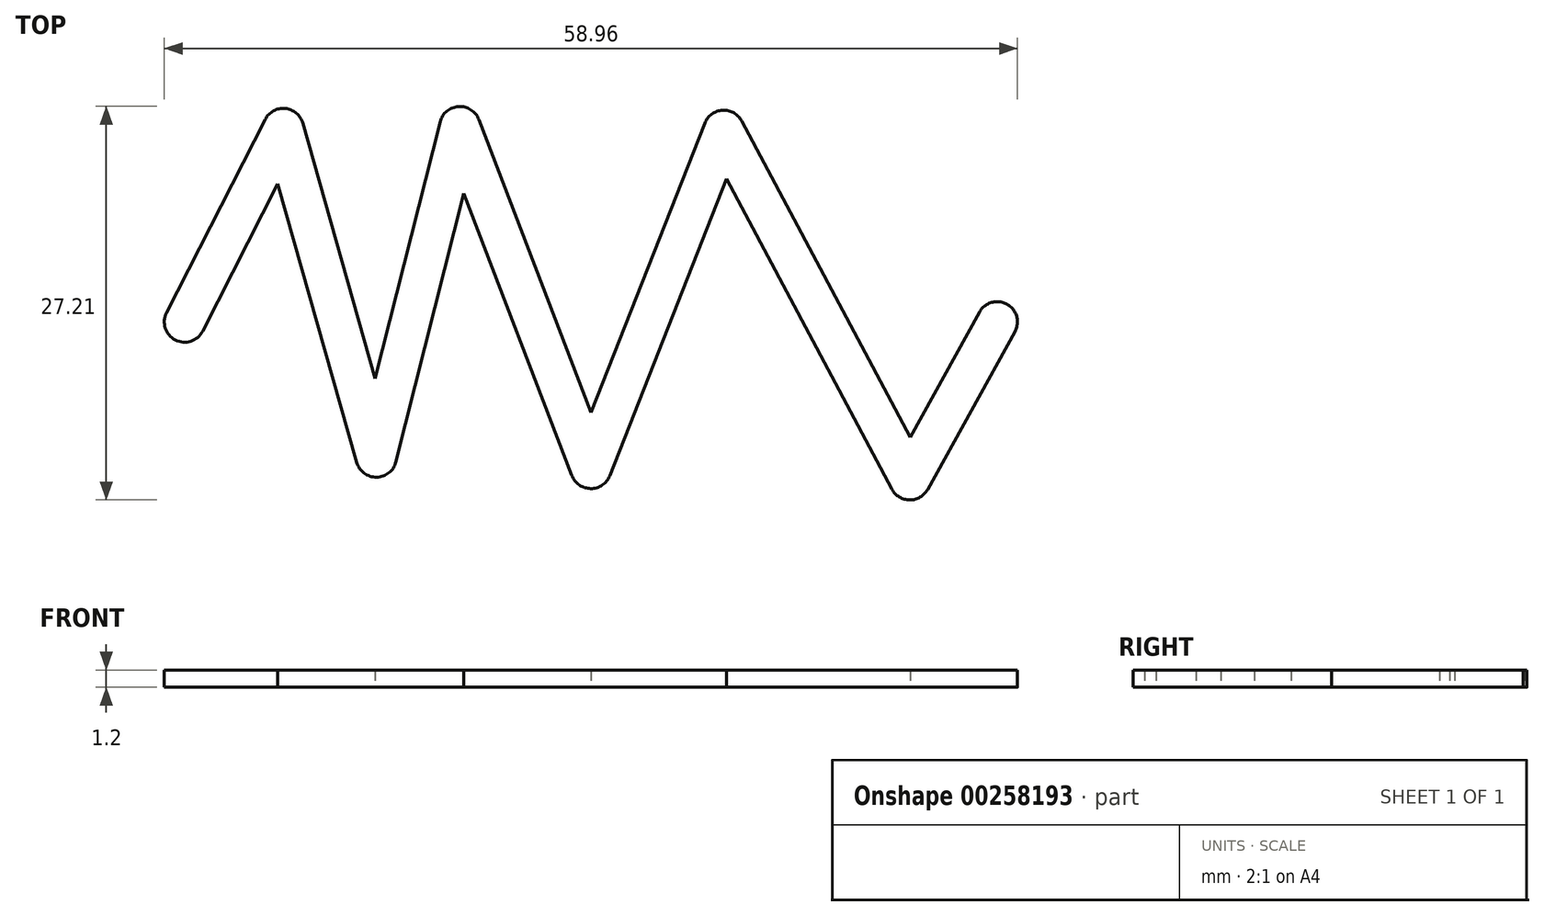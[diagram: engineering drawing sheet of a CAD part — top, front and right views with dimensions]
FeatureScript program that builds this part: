
annotation { "Feature Type Name" : "Feature", "Feature Type Description" : "" }
export const myFeature = defineFeature(function(context is Context, id is Id, definition is map)
    precondition{}
    {
        {
            var Q0;
            Q0=qCreatedBy(makeId("Top.planeOp"),FACE);
            var sketch = newSketch(context, id + "F0", { "sketchPlane" : qUnion([Q0])});
            skLineSegment(sketch, "E0", {"start": v(-42.58, 0) * mm, "end": v(-29.6, 0) * mm});
            skLineSegment(sketch, "E1", {"start": v(-29.6, 0) * mm, "end": v(-22.77, 13.37) * mm});
            skLineSegment(sketch, "E2", {"start": v(-22.77, 13.37) * mm, "end": v(-16.34, -9.33) * mm});
            skLineSegment(sketch, "E3", {"start": v(-16.34, -9.33) * mm, "end": v(-10.57, 13.5) * mm});
            skLineSegment(sketch, "E4", {"start": v(-10.57, 13.5) * mm, "end": v(-1.51, -10.12) * mm});
            skLineSegment(sketch, "E5", {"start": v(-1.51, -10.12) * mm, "end": v(7.67, 13.23) * mm});
            skLineSegment(sketch, "E6", {"start": v(7.67, 13.23) * mm, "end": v(20.53, -10.9) * mm});
            skLineSegment(sketch, "E7", {"start": v(20.53, -10.9) * mm, "end": v(26.57, 0) * mm});
            skLineSegment(sketch, "E8", {"start": v(26.57, 0) * mm, "end": v(42.18, 0) * mm});
            skArc(sketch, "E9.0.startCap", {"start": v(-24.12, 12.98) * mm, "mid": v(-23.15, 14.71) * mm, "end": v(-21.42, 13.75) * mm});
            skArc(sketch, "E9.0.endCap", {"start": v(-15, -8.95) * mm, "mid": v(-15.96, -10.68) * mm, "end": v(-17.69, -9.72) * mm});
            skLineSegment(sketch, "E9.0.left", {"start": v(-21.42, 13.75) * mm, "end": v(-15, -8.95) * mm});
            skLineSegment(sketch, "E9.0.right", {"start": v(-24.12, 12.98) * mm, "end": v(-17.69, -9.72) * mm});
            skArc(sketch, "E9.1.startCap", {"start": v(21.76, -11.59) * mm, "mid": v(19.85, -12.13) * mm, "end": v(19.3, -10.23) * mm});
            skArc(sketch, "E9.1.endCap", {"start": v(25.34, 0.68) * mm, "mid": v(27.25, 1.22) * mm, "end": v(27.8, -0.68) * mm});
            skLineSegment(sketch, "E9.1.left", {"start": v(19.3, -10.23) * mm, "end": v(25.34, 0.68) * mm});
            skLineSegment(sketch, "E9.1.right", {"start": v(21.76, -11.59) * mm, "end": v(27.8, -0.68) * mm});
            skArc(sketch, "E9.2.startCap", {"start": v(6.44, 12.58) * mm, "mid": v(7.02, 14.47) * mm, "end": v(8.9, 13.9) * mm});
            skArc(sketch, "E9.2.endCap", {"start": v(21.77, -10.25) * mm, "mid": v(21.2, -12.14) * mm, "end": v(19.3, -11.57) * mm});
            skLineSegment(sketch, "E9.2.left", {"start": v(8.9, 13.9) * mm, "end": v(21.77, -10.25) * mm});
            skLineSegment(sketch, "E9.2.right", {"start": v(6.44, 12.58) * mm, "end": v(19.3, -11.57) * mm});
            skArc(sketch, "E9.3.startCap", {"start": v(-14.98, -9.68) * mm, "mid": v(-16.68, -10.7) * mm, "end": v(-17.7, -9) * mm});
            skArc(sketch, "E9.3.endCap", {"start": v(-11.92, 13.84) * mm, "mid": v(-10.22, 14.85) * mm, "end": v(-9.2, 13.15) * mm});
            skLineSegment(sketch, "E9.3.left", {"start": v(-17.7, -9) * mm, "end": v(-11.92, 13.84) * mm});
            skLineSegment(sketch, "E9.3.right", {"start": v(-14.98, -9.68) * mm, "end": v(-9.2, 13.15) * mm});
            skArc(sketch, "E9.4.startCap", {"start": v(-0.2, -10.63) * mm, "mid": v(-2.02, -11.42) * mm, "end": v(-2.81, -9.6) * mm});
            skArc(sketch, "E9.4.endCap", {"start": v(6.37, 13.75) * mm, "mid": v(8.19, 14.54) * mm, "end": v(8.98, 12.72) * mm});
            skLineSegment(sketch, "E9.4.left", {"start": v(-2.81, -9.6) * mm, "end": v(6.37, 13.75) * mm});
            skLineSegment(sketch, "E9.4.right", {"start": v(-0.2, -10.63) * mm, "end": v(8.98, 12.72) * mm});
            skArc(sketch, "E9.5.startCap", {"start": v(26.57, -1.4) * mm, "mid": v(25.17, 0) * mm, "end": v(26.57, 1.4) * mm});
            skArc(sketch, "E9.5.endCap", {"start": v(42.18, 1.4) * mm, "mid": v(43.58, 0) * mm, "end": v(42.18, -1.4) * mm});
            skLineSegment(sketch, "E9.5.left", {"start": v(26.57, 1.4) * mm, "end": v(42.18, 1.4) * mm});
            skLineSegment(sketch, "E9.5.right", {"start": v(26.57, -1.4) * mm, "end": v(42.18, -1.4) * mm});
            skArc(sketch, "E9.6.startCap", {"start": v(-11.87, 13) * mm, "mid": v(-11.07, 14.8) * mm, "end": v(-9.26, 14) * mm});
            skArc(sketch, "E9.6.endCap", {"start": v(-0.2, -9.62) * mm, "mid": v(-1.01, -11.43) * mm, "end": v(-2.82, -10.62) * mm});
            skLineSegment(sketch, "E9.6.left", {"start": v(-9.26, 14) * mm, "end": v(-0.2, -9.62) * mm});
            skLineSegment(sketch, "E9.6.right", {"start": v(-11.87, 13) * mm, "end": v(-2.82, -10.62) * mm});
            skArc(sketch, "E9.7.startCap", {"start": v(-28.34, -0.64) * mm, "mid": v(-30.23, -1.25) * mm, "end": v(-30.84, 0.64) * mm});
            skArc(sketch, "E9.7.endCap", {"start": v(-24.02, 14) * mm, "mid": v(-22.13, 14.61) * mm, "end": v(-21.52, 12.73) * mm});
            skLineSegment(sketch, "E9.7.left", {"start": v(-30.84, 0.64) * mm, "end": v(-24.02, 14) * mm});
            skLineSegment(sketch, "E9.7.right", {"start": v(-28.34, -0.64) * mm, "end": v(-21.52, 12.73) * mm});
            skArc(sketch, "E9.8.startCap", {"start": v(-42.58, -1.4) * mm, "mid": v(-43.98, 0) * mm, "end": v(-42.58, 1.4) * mm});
            skArc(sketch, "E9.8.endCap", {"start": v(-29.6, 1.4) * mm, "mid": v(-28.2, 0) * mm, "end": v(-29.6, -1.4) * mm});
            skLineSegment(sketch, "E9.8.left", {"start": v(-42.58, 1.4) * mm, "end": v(-29.6, 1.4) * mm});
            skLineSegment(sketch, "E9.8.right", {"start": v(-42.58, -1.4) * mm, "end": v(-29.6, -1.4) * mm});
            skSolve(sketch);
        }
        {
            var Q0;
            {var subQ1=sQuery(id+"F0.wireOp",EDGE,"E9.2.startCap");Q0=makeQuery(id+"F0.imprint","IMPRINT",FACE,{"disambiguationData":[TD([[makeQuery(id+"F0.imprint","IMPRINT",EDGE,{"derivedFrom":subQ1}),1.0]])]});}
            var Q1;
            {var subQ0=sQuery(id+"F0.wireOp",EDGE,"E9.2.left");var subQ3=sQuery(id+"F0.wireOp",EDGE,"E7");var subQ4=makeQuery(id+"F0.imprint","INTERSECT",VERTEX,{"derivedFrom":[subQ3,subQ0]});Q1=makeQuery(id+"F0.imprint","IMPRINT",FACE,{"disambiguationData":[TD([[makeQuery(id+"F0.imprint","IMPRINT",EDGE,{"disambiguationData":[TD([[subQ4,-1.0]])],"derivedFrom":subQ3}),-1.0]])]});}
            var Q2;
            {var subQ0=sQuery(id+"F0.wireOp",EDGE,"E9.1.startCap");Q2=makeQuery(id+"F0.imprint","IMPRINT",FACE,{"disambiguationData":[TD([[makeQuery(id+"F0.imprint","IMPRINT",EDGE,{"derivedFrom":subQ0}),-1.0]])]});}
            var Q3;
            {var subQ0=sQuery(id+"F0.wireOp",EDGE,"E5");var subQ1=sQuery(id+"F0.wireOp",EDGE,"E4");var subQ2=makeQuery(id+"F0.imprint","INTERSECT",VERTEX,{"derivedFrom":[subQ1,subQ0]});Q3=makeQuery(id+"F0.imprint","IMPRINT",FACE,{"disambiguationData":[TD([[makeQuery(id+"F0.imprint","IMPRINT",EDGE,{"disambiguationData":[TD([[subQ2,1.0]])],"derivedFrom":subQ1}),1.0]])]});}
            var Q4;
            {var subQ0=sQuery(id+"F0.wireOp",EDGE,"E7");var subQ1=sQuery(id+"F0.wireOp",EDGE,"E6");var subQ2=makeQuery(id+"F0.imprint","INTERSECT",VERTEX,{"derivedFrom":[subQ1,subQ0]});Q4=makeQuery(id+"F0.imprint","IMPRINT",FACE,{"disambiguationData":[TD([[makeQuery(id+"F0.imprint","IMPRINT",EDGE,{"disambiguationData":[TD([[subQ2,1.0]])],"derivedFrom":subQ1}),1.0]])]});}
            var Q5;
            {var subQ3=sQuery(id+"F0.wireOp",EDGE,"E9.6.left");var subQ7=sQuery(id+"F0.wireOp",EDGE,"E5");var subQ9=makeQuery(id+"F0.imprint","INTERSECT",VERTEX,{"derivedFrom":[subQ7,subQ3]});Q5=makeQuery(id+"F0.imprint","IMPRINT",FACE,{"disambiguationData":[TD([[makeQuery(id+"F0.imprint","IMPRINT",EDGE,{"disambiguationData":[TD([[subQ9,-1.0]])],"derivedFrom":subQ7}),-1.0]])]});}
            var Q6;
            {var subQ2=sQuery(id+"F0.wireOp",EDGE,"E7");var subQ6=sQuery(id+"F0.wireOp",EDGE,"E8");var subQ8=makeQuery(id+"F0.imprint","INTERSECT",VERTEX,{"derivedFrom":[subQ2,subQ6]});Q6=makeQuery(id+"F0.imprint","IMPRINT",FACE,{"disambiguationData":[TD([[makeQuery(id+"F0.imprint","IMPRINT",EDGE,{"disambiguationData":[TD([[subQ8,1.0]])],"derivedFrom":subQ2}),1.0]])]});}
            var Q7;
            {var subQ0=sQuery(id+"F0.wireOp",EDGE,"E9.2.left");var subQ1=sQuery(id+"F0.wireOp",EDGE,"E7");var subQ2=makeQuery(id+"F0.imprint","INTERSECT",VERTEX,{"derivedFrom":[subQ1,subQ0]});Q7=makeQuery(id+"F0.imprint","IMPRINT",FACE,{"disambiguationData":[TD([[makeQuery(id+"F0.imprint","IMPRINT",EDGE,{"disambiguationData":[TD([[subQ2,-1.0]])],"derivedFrom":subQ1}),1.0]])]});}
            var Q8;
            {var subQ0=sQuery(id+"F0.wireOp",EDGE,"E9.2.startCap");Q8=makeQuery(id+"F0.imprint","IMPRINT",FACE,{"disambiguationData":[TD([[makeQuery(id+"F0.imprint","IMPRINT",EDGE,{"derivedFrom":subQ0}),-1.0]])]});}
            var Q9;
            {var subQ0=sQuery(id+"F0.wireOp",EDGE,"E4");var subQ1=sQuery(id+"F0.wireOp",EDGE,"E3");var subQ2=makeQuery(id+"F0.imprint","INTERSECT",VERTEX,{"derivedFrom":[subQ1,subQ0]});Q9=makeQuery(id+"F0.imprint","IMPRINT",FACE,{"disambiguationData":[TD([[makeQuery(id+"F0.imprint","IMPRINT",EDGE,{"disambiguationData":[TD([[subQ2,1.0]])],"derivedFrom":subQ1}),-1.0]])]});}
            var Q10;
            {var subQ1=sQuery(id+"F0.wireOp",EDGE,"E9.0.left");var subQ3=sQuery(id+"F0.wireOp",EDGE,"E3");var subQ4=makeQuery(id+"F0.imprint","INTERSECT",VERTEX,{"derivedFrom":[subQ3,subQ1]});Q10=makeQuery(id+"F0.imprint","IMPRINT",FACE,{"disambiguationData":[TD([[makeQuery(id+"F0.imprint","IMPRINT",EDGE,{"disambiguationData":[TD([[subQ4,-1.0]])],"derivedFrom":subQ3}),1.0]])]});}
            var Q11;
            {var subQ1=sQuery(id+"F0.wireOp",EDGE,"E9.3.endCap");Q11=makeQuery(id+"F0.imprint","IMPRINT",FACE,{"disambiguationData":[TD([[makeQuery(id+"F0.imprint","IMPRINT",EDGE,{"derivedFrom":subQ1}),-1.0]])]});}
            var Q12;
            {var subQ0=sQuery(id+"F0.wireOp",EDGE,"E9.3.endCap");Q12=makeQuery(id+"F0.imprint","IMPRINT",FACE,{"disambiguationData":[TD([[makeQuery(id+"F0.imprint","IMPRINT",EDGE,{"derivedFrom":subQ0}),1.0]])]});}
            var Q13;
            {var subQ0=sQuery(id+"F0.wireOp",EDGE,"E9.5.endCap");Q13=makeQuery(id+"F0.imprint","IMPRINT",FACE,{"disambiguationData":[TD([[makeQuery(id+"F0.imprint","IMPRINT",EDGE,{"derivedFrom":subQ0}),-1.0]])]});}
            var Q14;
            {var subQ0=sQuery(id+"F0.wireOp",EDGE,"E9.8.startCap");Q14=makeQuery(id+"F0.imprint","IMPRINT",FACE,{"disambiguationData":[TD([[makeQuery(id+"F0.imprint","IMPRINT",EDGE,{"derivedFrom":subQ0}),-1.0]])]});}
            var Q15;
            {var subQ2=sQuery(id+"F0.wireOp",EDGE,"E1");var subQ6=sQuery(id+"F0.wireOp",EDGE,"E0");var subQ8=makeQuery(id+"F0.imprint","INTERSECT",VERTEX,{"derivedFrom":[subQ6,subQ2]});Q15=makeQuery(id+"F0.imprint","IMPRINT",FACE,{"disambiguationData":[TD([[makeQuery(id+"F0.imprint","IMPRINT",EDGE,{"disambiguationData":[TD([[subQ8,1.0]])],"derivedFrom":subQ6}),-1.0]])]});}
            var Q16;
            {var subQ1=sQuery(id+"F0.wireOp",EDGE,"E9.0.startCap");Q16=makeQuery(id+"F0.imprint","IMPRINT",FACE,{"disambiguationData":[TD([[makeQuery(id+"F0.imprint","IMPRINT",EDGE,{"derivedFrom":subQ1}),1.0]])]});}
            var Q17;
            {var subQ0=sQuery(id+"F0.wireOp",EDGE,"E9.8.endCap");var subQ1=sQuery(id+"F0.wireOp",EDGE,"E1");var subQ2=makeQuery(id+"F0.imprint","INTERSECT",VERTEX,{"derivedFrom":[subQ1,subQ0]});Q17=makeQuery(id+"F0.imprint","IMPRINT",FACE,{"disambiguationData":[TD([[makeQuery(id+"F0.imprint","IMPRINT",EDGE,{"disambiguationData":[TD([[subQ2,-1.0]])],"derivedFrom":subQ1}),-1.0]])]});}
            var Q18;
            {var subQ6=sQuery(id+"F0.wireOp",EDGE,"E9.0.startCap");Q18=makeQuery(id+"F0.imprint","IMPRINT",FACE,{"disambiguationData":[TD([[makeQuery(id+"F0.imprint","IMPRINT",EDGE,{"derivedFrom":subQ6}),-1.0]])]});}
            var Q19;
            {var subQ0=sQuery(id+"F0.wireOp",EDGE,"E2");var subQ1=sQuery(id+"F0.wireOp",EDGE,"E1");var subQ2=makeQuery(id+"F0.imprint","INTERSECT",VERTEX,{"derivedFrom":[subQ1,subQ0]});Q19=makeQuery(id+"F0.imprint","IMPRINT",FACE,{"disambiguationData":[TD([[makeQuery(id+"F0.imprint","IMPRINT",EDGE,{"disambiguationData":[TD([[subQ2,1.0]])],"derivedFrom":subQ1}),-1.0]])]});}
            var Q20;
            {var subQ3=sQuery(id+"F0.wireOp",EDGE,"E9.7.right");var subQ7=sQuery(id+"F0.wireOp",EDGE,"E2");var subQ9=makeQuery(id+"F0.imprint","INTERSECT",VERTEX,{"derivedFrom":[subQ7,subQ3]});Q20=makeQuery(id+"F0.imprint","IMPRINT",FACE,{"disambiguationData":[TD([[makeQuery(id+"F0.imprint","IMPRINT",EDGE,{"disambiguationData":[TD([[subQ9,-1.0]])],"derivedFrom":subQ7}),1.0]])]});}
            var Q21;
            {var subQ3=sQuery(id+"F0.wireOp",EDGE,"E2");var subQ7=sQuery(id+"F0.wireOp",EDGE,"E9.7.right");var subQ8=makeQuery(id+"F0.imprint","INTERSECT",VERTEX,{"derivedFrom":[subQ3,subQ7]});Q21=makeQuery(id+"F0.imprint","IMPRINT",FACE,{"disambiguationData":[TD([[makeQuery(id+"F0.imprint","IMPRINT",EDGE,{"disambiguationData":[TD([[subQ8,-1.0]])],"derivedFrom":subQ3}),-1.0]])]});}
            var Q22;
            {var subQ0=sQuery(id+"F0.wireOp",EDGE,"E9.0.endCap");Q22=makeQuery(id+"F0.imprint","IMPRINT",FACE,{"disambiguationData":[TD([[makeQuery(id+"F0.imprint","IMPRINT",EDGE,{"derivedFrom":subQ0}),-1.0]])]});}
            var Q23;
            {var subQ0=sQuery(id+"F0.wireOp",EDGE,"E3");var subQ1=sQuery(id+"F0.wireOp",EDGE,"E2");var subQ2=makeQuery(id+"F0.imprint","INTERSECT",VERTEX,{"derivedFrom":[subQ1,subQ0]});Q23=makeQuery(id+"F0.imprint","IMPRINT",FACE,{"disambiguationData":[TD([[makeQuery(id+"F0.imprint","IMPRINT",EDGE,{"disambiguationData":[TD([[subQ2,1.0]])],"derivedFrom":subQ1}),1.0]])]});}
            var Q24;
            {var subQ1=sQuery(id+"F0.wireOp",EDGE,"E9.0.endCap");Q24=makeQuery(id+"F0.imprint","IMPRINT",FACE,{"disambiguationData":[TD([[makeQuery(id+"F0.imprint","IMPRINT",EDGE,{"derivedFrom":subQ1}),1.0]])]});}
            var Q25;
            {var subQ0=sQuery(id+"F0.wireOp",EDGE,"E6");var subQ1=sQuery(id+"F0.wireOp",EDGE,"E5");var subQ2=makeQuery(id+"F0.imprint","INTERSECT",VERTEX,{"derivedFrom":[subQ1,subQ0]});Q25=makeQuery(id+"F0.imprint","IMPRINT",FACE,{"disambiguationData":[TD([[makeQuery(id+"F0.imprint","IMPRINT",EDGE,{"disambiguationData":[TD([[subQ2,1.0]])],"derivedFrom":subQ1}),-1.0]])]});}
            var Q26;
            {var subQ0=sQuery(id+"F0.wireOp",EDGE,"E9.4.startCap");Q26=makeQuery(id+"F0.imprint","IMPRINT",FACE,{"disambiguationData":[TD([[makeQuery(id+"F0.imprint","IMPRINT",EDGE,{"derivedFrom":subQ0}),1.0]])]});}
            var Q27;
            {var subQ1=sQuery(id+"F0.wireOp",EDGE,"E9.1.startCap");Q27=makeQuery(id+"F0.imprint","IMPRINT",FACE,{"disambiguationData":[TD([[makeQuery(id+"F0.imprint","IMPRINT",EDGE,{"derivedFrom":subQ1}),1.0]])]});}
            var Q28;
            {var subQ1=sQuery(id+"F0.wireOp",EDGE,"E9.4.startCap");Q28=makeQuery(id+"F0.imprint","IMPRINT",FACE,{"disambiguationData":[TD([[makeQuery(id+"F0.imprint","IMPRINT",EDGE,{"derivedFrom":subQ1}),-1.0]])]});}
            var Q29;
            {var subQ3=sQuery(id+"F0.wireOp",EDGE,"E9.4.right");var subQ7=sQuery(id+"F0.wireOp",EDGE,"E6");var subQ9=makeQuery(id+"F0.imprint","INTERSECT",VERTEX,{"derivedFrom":[subQ7,subQ3]});Q29=makeQuery(id+"F0.imprint","IMPRINT",FACE,{"disambiguationData":[TD([[makeQuery(id+"F0.imprint","IMPRINT",EDGE,{"disambiguationData":[TD([[subQ9,-1.0]])],"derivedFrom":subQ7}),1.0]])]});}
            var Q30;
            {var subQ5=sQuery(id+"F0.wireOp",EDGE,"E0");var subQ7=sQuery(id+"F0.wireOp",EDGE,"E1");var subQ8=makeQuery(id+"F0.imprint","INTERSECT",VERTEX,{"derivedFrom":[subQ5,subQ7]});Q30=makeQuery(id+"F0.imprint","IMPRINT",FACE,{"disambiguationData":[TD([[makeQuery(id+"F0.imprint","IMPRINT",EDGE,{"disambiguationData":[TD([[subQ8,1.0]])],"derivedFrom":subQ5}),1.0]])]});}
            var Q31;
            {var subQ7=sQuery(id+"F0.wireOp",EDGE,"E8");var subQ9=sQuery(id+"F0.wireOp",EDGE,"E7");var subQ10=makeQuery(id+"F0.imprint","INTERSECT",VERTEX,{"derivedFrom":[subQ9,subQ7]});Q31=makeQuery(id+"F0.imprint","IMPRINT",FACE,{"disambiguationData":[TD([[makeQuery(id+"F0.imprint","IMPRINT",EDGE,{"disambiguationData":[TD([[subQ10,1.0]])],"derivedFrom":subQ9}),-1.0]])]});}
            extrude(context, id + "F1", {"entities" : qUnion([Q0, Q1, Q2, Q3, Q4, Q5, Q6, Q7, Q8, Q9, Q10, Q11, Q12, Q13, Q14, Q15, Q16, Q17, Q18, Q19, Q20, Q21, Q22, Q23, Q24, Q25, Q26, Q27, Q28, Q29, Q30, Q31]), "depth" : 1.2 * mm});
        }
    });
